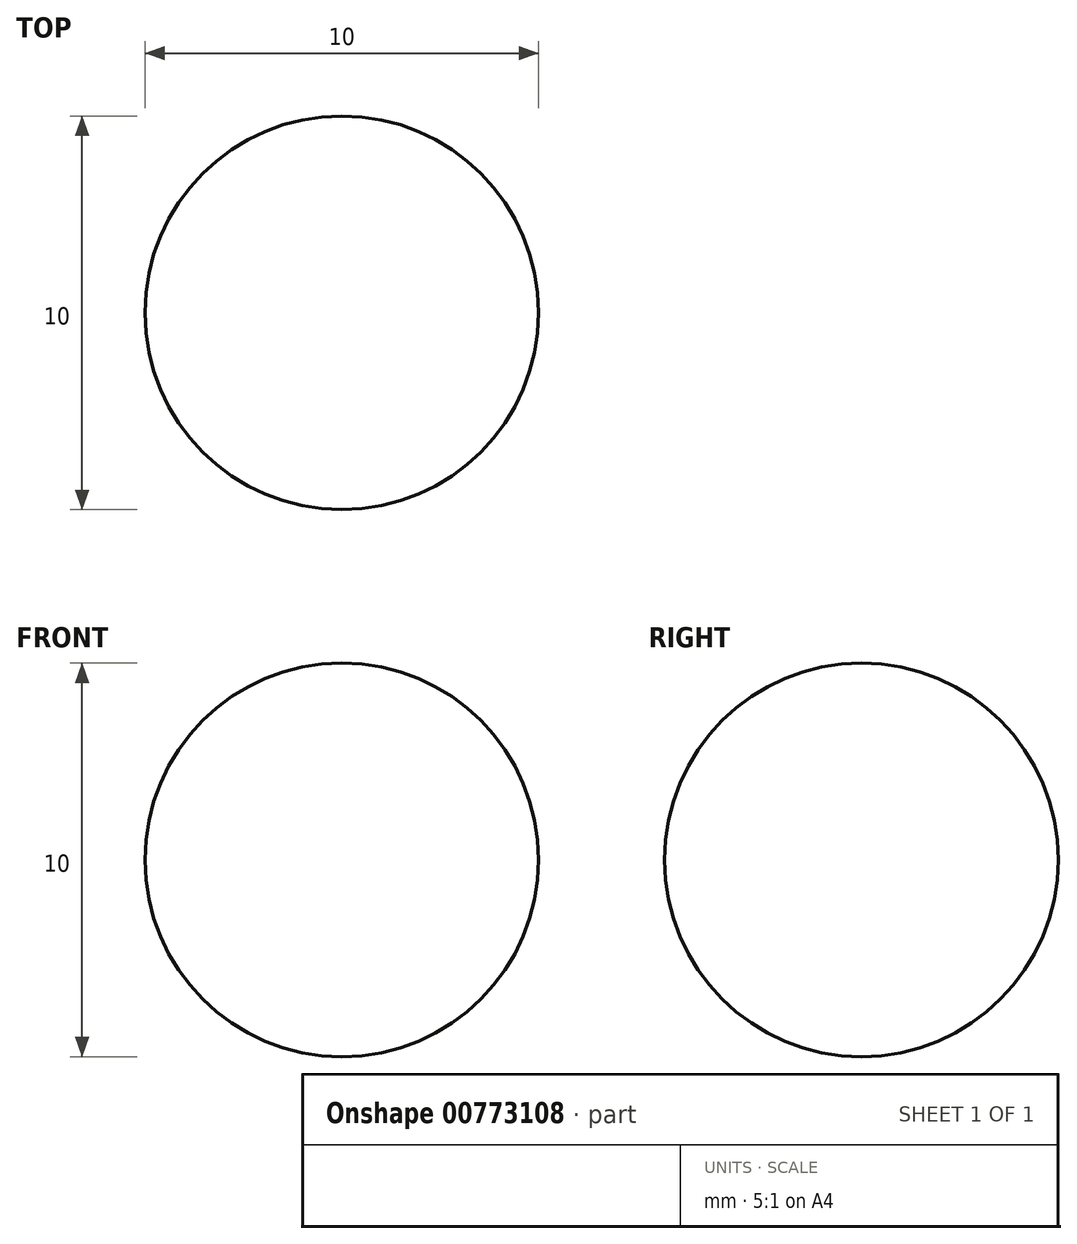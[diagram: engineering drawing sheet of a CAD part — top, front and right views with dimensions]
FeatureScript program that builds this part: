
annotation { "Feature Type Name" : "Feature", "Feature Type Description" : "" }
export const myFeature = defineFeature(function(context is Context, id is Id, definition is map)
    precondition{}
    {
        {
            var Q0;
            Q0=qCreatedBy(makeId("Front.planeOp"),FACE);
            var sketch = newSketch(context, id + "F0", { "sketchPlane" : qUnion([Q0])});
            skLineSegment(sketch, "E0", {"start": v(0, 5) * mm, "end": v(0, -5) * mm});
            skArc(sketch, "E1", {"start": v(0, -5) * mm, "mid": v(5, 0) * mm, "end": v(0, 5) * mm});
            skSolve(sketch);
        }
        {
            var Q0;
            Q0 = qSketchRegion(id + "F0", true);
            var Q1;
            Q1=sQuery(id+"F0.wireOp",EDGE,"E0");
            revolve(context, id + "F1", {"surfaceOperationType" : NewSurfaceOperationType.NEW, "entities" : qUnion([Q0]), "axis" : qUnion([Q1]), "revolveType" : RevolveType.FULL});
        }
    });
